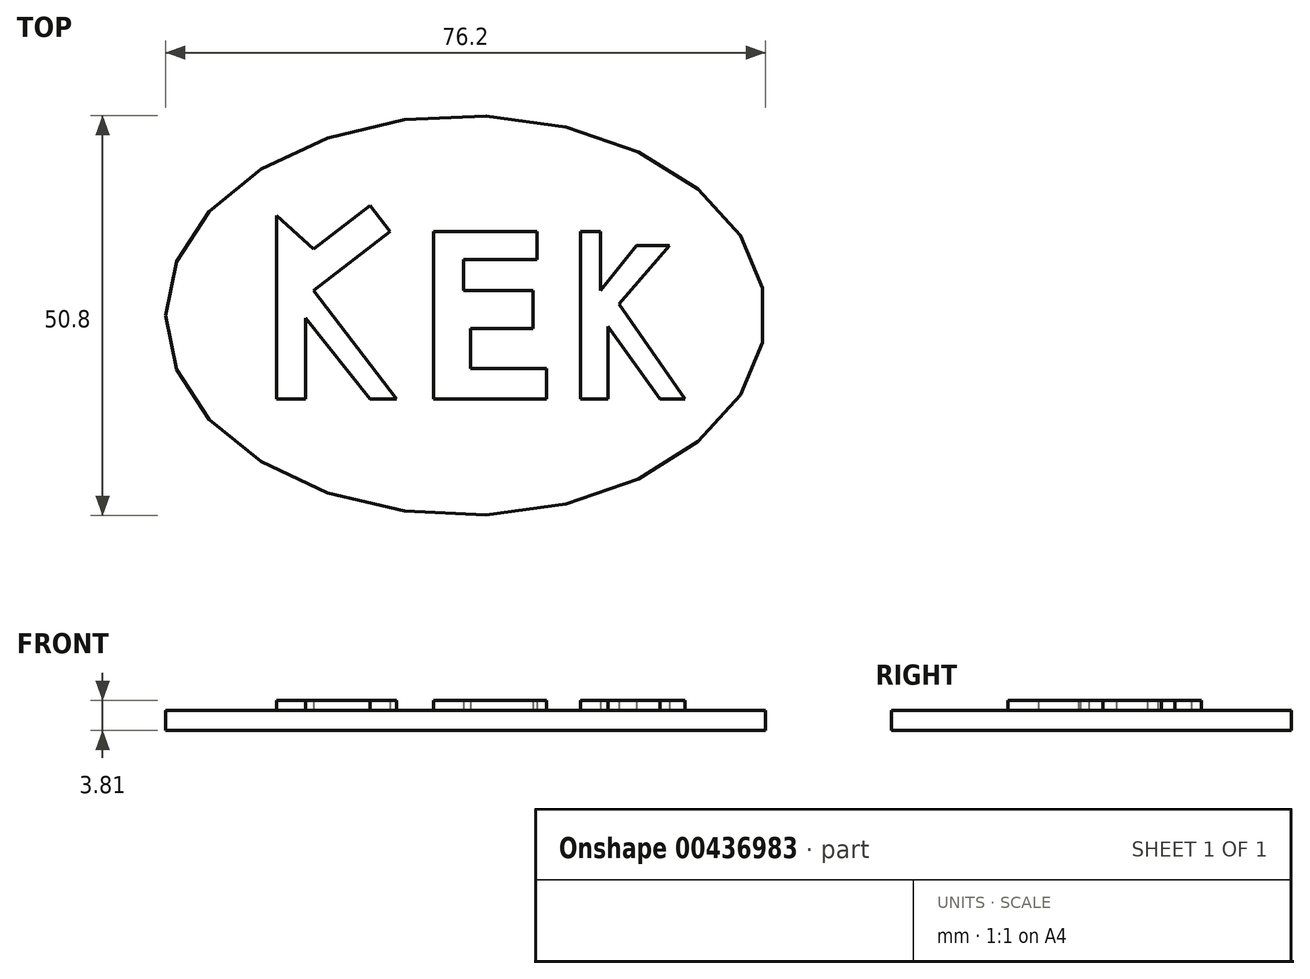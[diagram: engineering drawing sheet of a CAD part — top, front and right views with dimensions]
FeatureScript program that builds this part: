
annotation { "Feature Type Name" : "Feature", "Feature Type Description" : "" }
export const myFeature = defineFeature(function(context is Context, id is Id, definition is map)
    precondition{}
    {
        {
            var Q0;
            Q0=qCreatedBy(makeId("Top.planeOp"),FACE);
            var sketch = newSketch(context, id + "F0", { "sketchPlane" : qUnion([Q0])});
            skEllipse(sketch, "E0", {"center": v(-7.37, 9.12) * mm, "majorRadius": 38.1 * mm, "minorRadius": 25.4 * mm, "majorAxis": v(-1, 0)});
            skSolve(sketch);
        }
        {
            var Q0;
            Q0 = qSketchRegion(id + "F0", true);
            extrude(context, id + "F1", {"entities" : qUnion([Q0]), "depth" : 2.54 * mm});
        }
        {
            var Q0;
            Q0=qCreatedBy(makeId("Top.planeOp"),FACE);
            var sketch = newSketch(context, id + "F2", { "sketchPlane" : qUnion([Q0])});
            skLineSegment(sketch, "E1", {"start": v(-31.4, 21.83) * mm, "end": v(-31.4, -1.47) * mm});
            skLineSegment(sketch, "E2", {"start": v(-31.4, -1.47) * mm, "end": v(-27.68, -1.47) * mm});
            skLineSegment(sketch, "E3", {"start": v(-27.68, -1.47) * mm, "end": v(-27.68, 8.82) * mm});
            skLineSegment(sketch, "E4", {"start": v(-27.68, 8.82) * mm, "end": v(-19.5, -1.47) * mm});
            skLineSegment(sketch, "E5", {"start": v(-19.5, -1.47) * mm, "end": v(-16.15, -1.47) * mm});
            skLineSegment(sketch, "E6", {"start": v(-16.15, -1.47) * mm, "end": v(-26.69, 12.29) * mm});
            skLineSegment(sketch, "E7", {"start": v(-26.69, 12.29) * mm, "end": v(-16.94, 19.75) * mm});
            skLineSegment(sketch, "E8", {"start": v(-16.94, 19.75) * mm, "end": v(-19.5, 23.1) * mm});
            skLineSegment(sketch, "E9", {"start": v(-19.5, 23.1) * mm, "end": v(-26.69, 17.59) * mm});
            skLineSegment(sketch, "E10", {"start": v(-26.69, 17.59) * mm, "end": v(-31.4, 21.83) * mm});
            skLineSegment(sketch, "E11", {"start": v(-11.45, 19.75) * mm, "end": v(-11.45, -1.47) * mm});
            skLineSegment(sketch, "E12", {"start": v(-11.45, -1.47) * mm, "end": v(2.93, -1.47) * mm});
            skLineSegment(sketch, "E13", {"start": v(2.93, -1.47) * mm, "end": v(2.93, 2.37) * mm});
            skLineSegment(sketch, "E14", {"start": v(2.93, 2.37) * mm, "end": v(-6.74, 2.37) * mm});
            skLineSegment(sketch, "E15", {"start": v(-6.74, 2.37) * mm, "end": v(-6.74, 7.45) * mm});
            skLineSegment(sketch, "E16", {"start": v(-6.74, 7.45) * mm, "end": v(1.2, 7.45) * mm});
            skLineSegment(sketch, "E17", {"start": v(1.2, 7.45) * mm, "end": v(1.2, 12.29) * mm});
            skLineSegment(sketch, "E18", {"start": v(1.2, 12.29) * mm, "end": v(-7.6, 12.29) * mm});
            skLineSegment(sketch, "E19", {"start": v(-7.6, 12.29) * mm, "end": v(-7.6, 16.25) * mm});
            skLineSegment(sketch, "E20", {"start": v(-7.6, 16.25) * mm, "end": v(1.69, 16.25) * mm});
            skLineSegment(sketch, "E21", {"start": v(1.69, 16.25) * mm, "end": v(1.69, 19.75) * mm});
            skLineSegment(sketch, "E22", {"start": v(1.69, 19.75) * mm, "end": v(-11.45, 19.75) * mm});
            skLineSegment(sketch, "E23", {"start": v(7.26, 19.75) * mm, "end": v(7.26, -1.47) * mm});
            skLineSegment(sketch, "E24", {"start": v(7.26, -1.47) * mm, "end": v(10.73, -1.47) * mm});
            skLineSegment(sketch, "E25", {"start": v(10.73, -1.47) * mm, "end": v(10.73, 7.7) * mm});
            skLineSegment(sketch, "E26", {"start": v(10.73, 7.7) * mm, "end": v(17.3, -1.47) * mm});
            skLineSegment(sketch, "E27", {"start": v(17.3, -1.47) * mm, "end": v(20.52, -1.47) * mm});
            skLineSegment(sketch, "E28", {"start": v(20.52, -1.47) * mm, "end": v(12.1, 10.55) * mm});
            skLineSegment(sketch, "E29", {"start": v(12.1, 10.55) * mm, "end": v(18.54, 17.99) * mm});
            skLineSegment(sketch, "E30", {"start": v(18.54, 17.99) * mm, "end": v(14.33, 17.99) * mm});
            skLineSegment(sketch, "E31", {"start": v(14.33, 17.99) * mm, "end": v(9.74, 12.29) * mm});
            skLineSegment(sketch, "E32", {"start": v(9.74, 12.29) * mm, "end": v(9.74, 19.75) * mm});
            skLineSegment(sketch, "E33", {"start": v(9.74, 19.75) * mm, "end": v(7.26, 19.75) * mm});
            skSolve(sketch);
        }
        {
            var Q0;
            Q0 = qSketchRegion(id + "F2", true);
            extrude(context, id + "F3", {"entities" : qUnion([Q0]), "operationType" : NewBodyOperationType.ADD, "depth" : 3.8 * mm});
        }
    });
